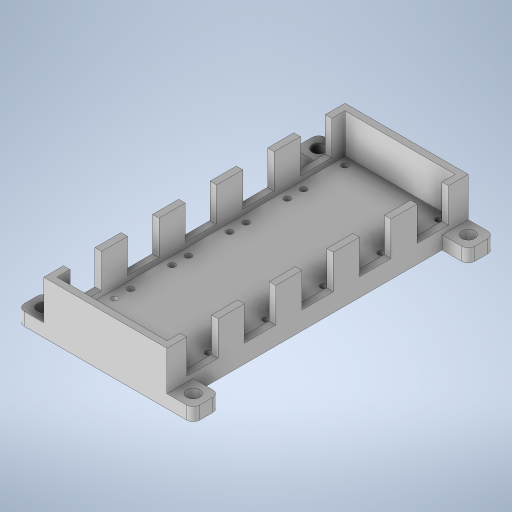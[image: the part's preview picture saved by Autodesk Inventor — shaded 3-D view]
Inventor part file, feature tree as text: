
AUTODESK INVENTOR PART (.ipt)
format: ipt  version: 2024 (Build 280153000, 153)  size: 947,712 bytes
history: native  units: in
note: dims shown in document units (in); Inventor stores cm internally (conversion verified against a paired STEP export)
features: projected_geometry x13, extrude x5, sketch x4
ambient origin geometry x8: Origin, YZ Plane, XZ Plane, XY Plane, X Axis, Y Axis, Z Axis, Center Point
bodies: Solid1 (feature_tree)
feature tree (22):
  extrude  "Extrusion1"  Depth=1.0in
  extrude  "Extrusion7"  Depth=0.0742in
  extrude  "Extrusion8"  Depth=0.2in
  extrude  "Extrusion9"  Depth=0.125in
  extrude  "Extrusion10"  Depth=0.125in
  sketch  "Sketch10"  dims[d0=1.0in d1=2.0in]
  projected_geometry  "Projected Loop17"
  sketch  "Sketch11"  dims[d2=0.12in d3=0.0742in]
  projected_geometry  "Projected Loop18"
  projected_geometry  "Projected Loop19"
  projected_geometry  "Projected Loop20"
  projected_geometry  "Projected Loop21"
  projected_geometry  "Projected Loop22"
  projected_geometry  "Projected Loop23"
  projected_geometry  "Projected Loop24"
  projected_geometry  "Projected Loop25"
  projected_geometry  "Projected Loop26"
  projected_geometry  "Projected Loop27"
  sketch  "Sketch12"  dims[d4=0.1742in d5=0.2in]
  projected_geometry  "Projected Loop28"
  sketch  "Sketch13"  dims[d6=0.2in d7=0.201in d8=0.799in d9=0.8in d10=0.8in d11=0.3in d12=0.4967in d13=0.4267in d14=0.1217in d15=0.3933in d16=1.3983in d17=1.0933in d18=0.7933in d19=0.4967in d20=0.0in d21=1.5033in d22=0.0in d23=0.0in d24=0.0742in d25=0.3in d26=0.0742in d27=0.105in d28=0.3949in d29=0.105in d30=1.4015in d31=0.0in d32=0.1742in d33=0.3in d34=0.1742in d35=0.4267in d36=0.2in d37=0.1217in d38=0.2in d39=0.2in d40=1.0933in d41=0.2in d42=1.3983in d43=0.3933in d44=0.201in d45=0.201in d46=1.0933in d47=0.3933in d48=0.799in d49=1.0933in d50=0.799in d51=0.4267in d52=0.8in d53=0.1217in d54=0.8in d55=0.8in d56=1.0933in d57=0.8in d58=1.3983in d59=0.895in d60=0.3949in d61=0.895in d62=1.4015in d63=1.0in d64=0.4967in d65=1.5033in d66=1.0in d67=1.0in d68=2.0in d69=0.12in d70=0.0742in d71=0.1742in d72=0.2in d73=0.2in d74=0.201in d75=0.799in d76=0.8in d77=0.8in d78=0.3in d79=0.4967in d80=0.4267in d81=0.1217in d82=0.3933in d83=1.3983in d84=1.0933in d85=0.7933in d86=0.4967in d87=0.0in d88=1.5033in d89=0.0in d90=0.0in d91=0.0742in d92=0.3in d93=0.0742in d94=0.105in d95=0.3949in d96=0.105in d97=1.4015in d98=0.0in d99=0.1742in d100=0.3in d101=0.1742in d102=0.4267in d103=0.2in d104=0.1217in d105=0.2in d106=0.2in d107=1.0933in d108=0.2in d109=1.3983in d110=0.3933in d111=0.201in d112=0.201in d113=1.0933in d114=0.3933in d115=0.799in d116=1.0933in d117=0.799in d118=0.4267in d119=0.8in d120=0.1217in d121=0.8in d122=0.8in d123=1.0933in d124=0.8in d125=1.3983in d126=0.895in d127=0.3949in d128=0.895in d129=1.4015in d130=1.0in d131=0.4967in d132=1.5033in d133=1.0in d134=1.0in d135=2.0in d136=0.12in d137=0.0742in d138=0.1742in d139=0.2in d140=0.2in d141=0.201in d142=0.799in d143=0.8in d144=0.8in d145=0.3in d146=0.4967in d147=0.4267in d148=0.1217in d149=0.3933in d150=1.3983in d151=1.0933in d152=0.7933in d153=0.4967in d154=0.0in d155=1.5033in d156=0.0in d157=0.0in d158=0.0742in d159=0.3in d160=0.0742in d161=0.105in d162=0.3949in d163=0.105in d164=1.4015in d165=0.0in d166=0.1742in d167=0.3in d168=0.1742in d169=0.4267in d170=0.2in d171=0.1217in d172=0.2in d173=0.2in d174=1.0933in d175=0.2in d176=1.3983in d177=0.3933in d178=0.201in d179=0.201in d180=1.0933in d181=0.3933in d182=0.799in d183=1.0933in d184=0.799in d185=0.4267in d186=0.8in d187=0.1217in d188=0.8in d189=0.8in d190=1.0933in d191=0.8in d192=1.3983in d193=0.895in d194=0.3949in d195=0.895in d196=1.4015in d197=1.0in d198=0.4967in d199=1.5033in d200=1.0in d201=1.0in d202=2.0in d203=0.12in d204=0.0742in d205=0.1742in d206=0.2in d207=0.2in d208=0.201in d209=0.799in d210=0.8in d211=0.8in d212=0.3in d213=0.4967in d214=0.4267in d215=0.1217in d216=0.3933in d217=1.3983in d218=1.0933in d219=0.7933in d220=0.4967in d221=0.0in d222=1.5033in d223=0.0in d224=0.0in d225=0.0742in d226=0.3in d227=0.0742in d228=0.105in d229=0.3949in d230=0.105in d231=1.4015in d232=0.0in d233=0.1742in d234=0.3in d235=0.1742in d236=0.4267in d237=0.2in d238=0.1217in d239=0.2in d240=0.2in d241=1.0933in d242=0.2in d243=1.3983in d244=0.3933in d245=0.201in d246=0.201in d247=1.0933in d248=0.3933in d249=0.799in d250=1.0933in d251=0.799in d252=0.4267in d253=0.8in d254=0.1217in d255=0.8in d256=0.8in d257=1.0933in d258=0.8in d259=1.3983in d260=0.895in d261=0.3949in d262=0.895in d263=1.4015in d264=1.0in d265=0.4967in d266=1.5033in d267=1.0in d268=1.0in d269=2.0in d270=0.12in d271=0.0742in d272=0.1742in d273=0.2in d274=0.2in d275=0.201in d276=0.799in d277=0.8in d278=0.8in d279=0.3in d280=0.4967in d281=0.4267in d282=0.1217in d283=0.3933in d284=1.3983in d285=1.0933in d286=0.7933in d287=0.4967in d288=0.0in d289=1.5033in d290=0.0in d291=0.0in d292=0.0742in d293=0.3in d294=0.0742in d295=0.105in d296=0.3949in d297=0.105in d298=1.4015in d299=0.0in d300=0.1742in d301=0.3in d302=0.1742in d303=0.4267in d304=0.2in d305=0.1217in d306=0.2in d307=0.2in d308=1.0933in d309=0.2in d310=1.3983in d311=0.3933in d312=0.201in d313=0.201in d314=1.0933in d315=0.3933in d316=0.799in d317=1.0933in d318=0.799in d319=0.4267in d320=0.8in d321=0.1217in d322=0.8in d323=0.8in d324=1.0933in d325=0.8in d326=1.3983in d327=0.895in d328=0.3949in d329=0.895in d330=1.4015in d331=1.0in d332=0.4967in d333=1.5033in d334=1.0in d335=0.1in d336=0.1in d337=0.1in d338=0.1in d339=0.03in d340=0.03in d341=0.125in d342=0.0in d367=0.125in d368=0.75in d369=0.0in d370=0.1in d371=0.0in d372=0.5in d373=0.5in d374=0.5in d375=0.5in d376=0.25in d377=0.25in d378=0.125in d379=0.125in d380=0.0in d381=0.125in d382=0.125in d383=0.0in]
  projected_geometry  "Projected Loop29"
